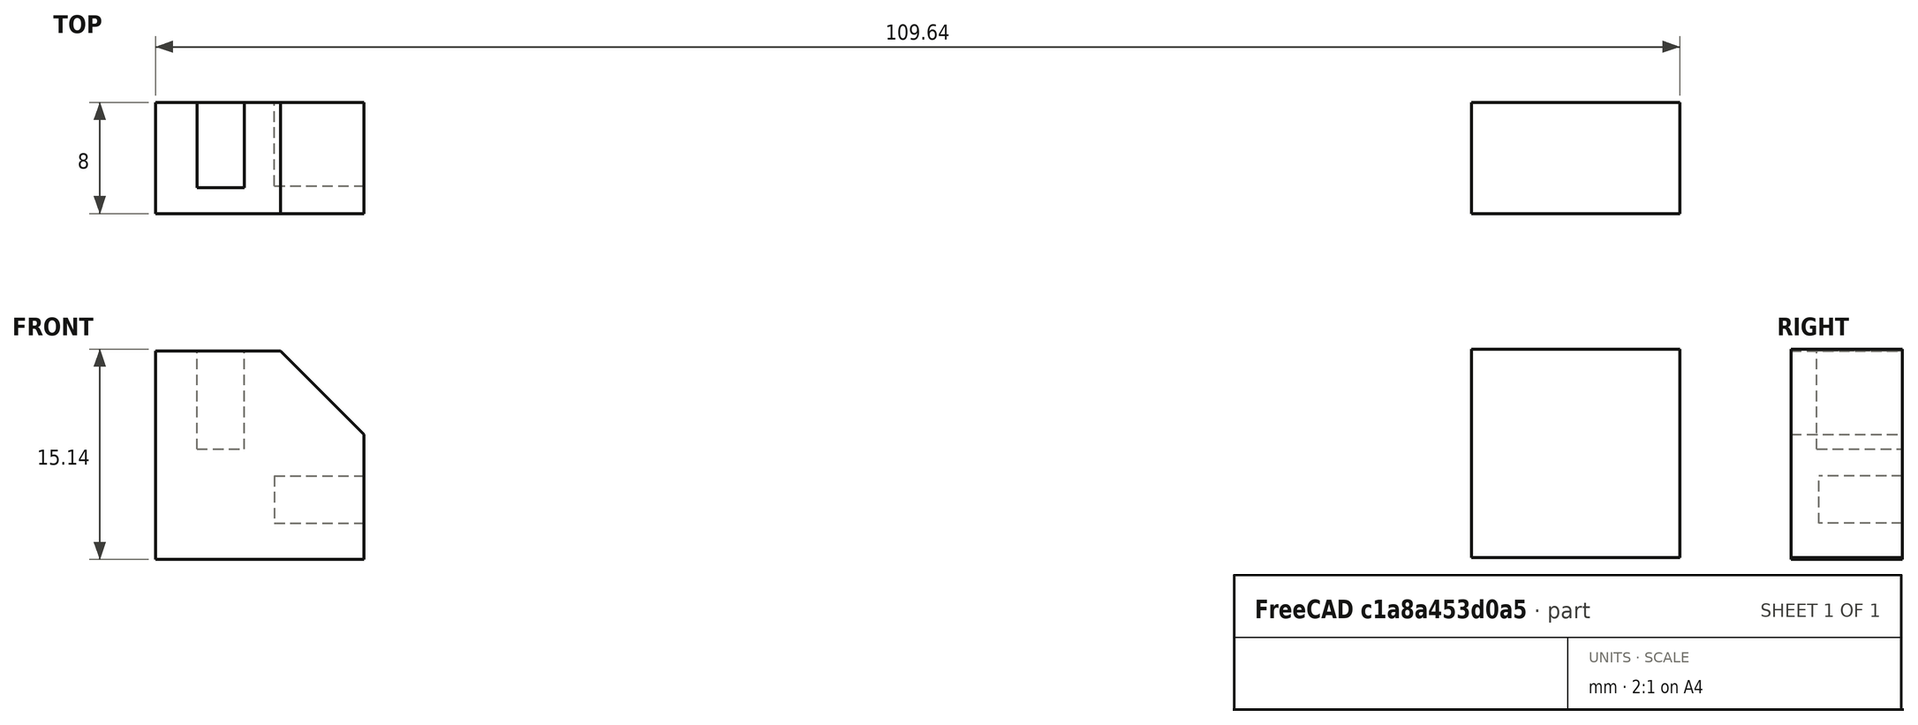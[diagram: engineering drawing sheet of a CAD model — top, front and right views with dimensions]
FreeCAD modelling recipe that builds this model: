
FCSTD DOCUMENT  (FreeCAD 0.14R3702 (Git))
Label: estanteria_disquette
License: CC-BY 3.0
LicenseURL: http://creativecommons.org/licenses/by/3.0/
objects: Part::Box×3, Part::FeaturePython×3, PartDesign::Chamfer×1, Part::MultiFuse×1, Part::Cut×1
note: 9 computed .brp shape members not serialized (recipe doc carries the construction recipe); baked Part::Feature solids carry a one-line shape summary decoded from their .brp

FEATURE [Part::Box] Box  label="Cubo"
  Height = 3.4
  Length = 90
  Width = 93.7
FEATURE [Part::FeaturePython] Array  # Draft array (typed FeaturePython)
  Angle = 360
  ArrayType = 0
  Axis = (1,1,1)
  Base = -> Box
  Center = (0,0,0)
  IntervalX = (97.7,0,0)
  IntervalY = (0,98.7,0)
  IntervalZ = (0,0,97.7)
  NumberPolar = 1
  NumberX = 2
  NumberY = 1
  NumberZ = 3
FEATURE [Part::FeaturePython] Clone  label="Clone of Cubo"  # Draft clone (typed FeaturePython)
  Objects = -> [Box]
  Placement = pos=(-0.3,-0.15,3.4) rot=(0,-1,0;1.5708rad)
  Scale = (1,1,1)
FEATURE [Part::FeaturePython] Array001  # Draft array (typed FeaturePython)
  Angle = 360
  ArrayType = 0
  Axis = (0,0,1)
  Base = -> Clone
  Center = (0,0,0)
  IntervalX = (97.7,0,0)
  IntervalY = (0,97.7,0)
  IntervalZ = (0,0,97.7)
  NumberPolar = 1
  NumberX = 3
  NumberY = 2
  NumberZ = 2
  Placement = pos=(-1.85702,-3.2783e-08,1.93209) rot=(0,0,1;0rad)
FEATURE [Part::Box] Box001  label="Cubo001"
  Height = 15
  Length = 15
  Placement = pos=(-8.55343,-2,-2.60887) rot=(0,0,1;0rad)
  Width = 8
FEATURE [PartDesign::Chamfer] Chamfer
  Base = -> Box001 [Edge6]
  Placement = pos=(-8.55343,-2,-2.60887) rot=(0,0,1;0rad)
  Size = 6
FEATURE [Part::MultiFuse] Fusion
  Shapes = -> [Array,Array001]
FEATURE [Part::Cut] Cut
  Base = -> Chamfer
  Tool = -> Fusion
FEATURE [Part::Box] Box002  label="Cubo002"
  Height = 15
  Length = 15
  Placement = pos=(86.0938,-2,-2.47137) rot=(0,0,1;0rad)
  Width = 8
